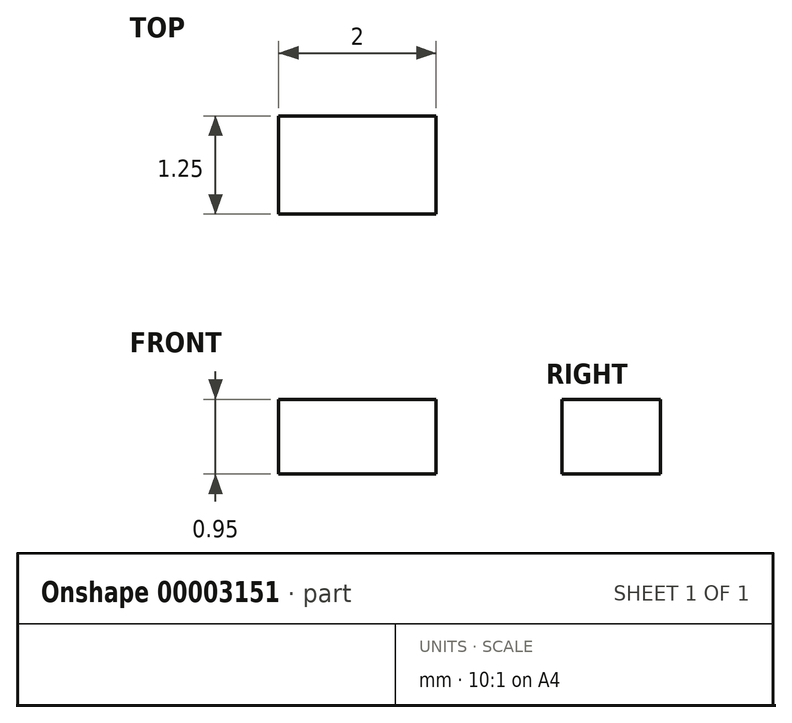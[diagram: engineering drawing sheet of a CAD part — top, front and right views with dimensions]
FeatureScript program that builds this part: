
annotation { "Feature Type Name" : "Feature", "Feature Type Description" : "" }
export const myFeature = defineFeature(function(context is Context, id is Id, definition is map)
    precondition{}
    {
        {
            var Q0;
            Q0=qCreatedBy(makeId("Top.planeOp"),FACE);
            var sketch = newSketch(context, id + "F0", { "sketchPlane" : qUnion([Q0])});
            skLineSegment(sketch, "E0.bottom", {"start": v(-1.54, 1.3) * mm, "end": v(0.46, 1.3) * mm});
            skLineSegment(sketch, "E0.top", {"start": v(-1.54, 0.06) * mm, "end": v(0.46, 0.06) * mm});
            skLineSegment(sketch, "E0.left", {"start": v(-1.54, 1.3) * mm, "end": v(-1.54, 0.06) * mm});
            skLineSegment(sketch, "E0.right", {"start": v(0.46, 1.3) * mm, "end": v(0.46, 0.06) * mm});
            skSolve(sketch);
        }
        {
            var Q0;
            Q0=makeQuery(id+"F0.imprint","IMPRINT",FACE,{"disambiguationData":[TD([[makeQuery(id+"F0.imprint","IMPRINT",EDGE,{"derivedFrom":sQuery(id+"F0.wireOp",EDGE,"E0.bottom")}),-1.0]])]});
            extrude(context, id + "F1", {"entities" : qUnion([Q0]), "depth" : .95 * mm});
        }
    });
